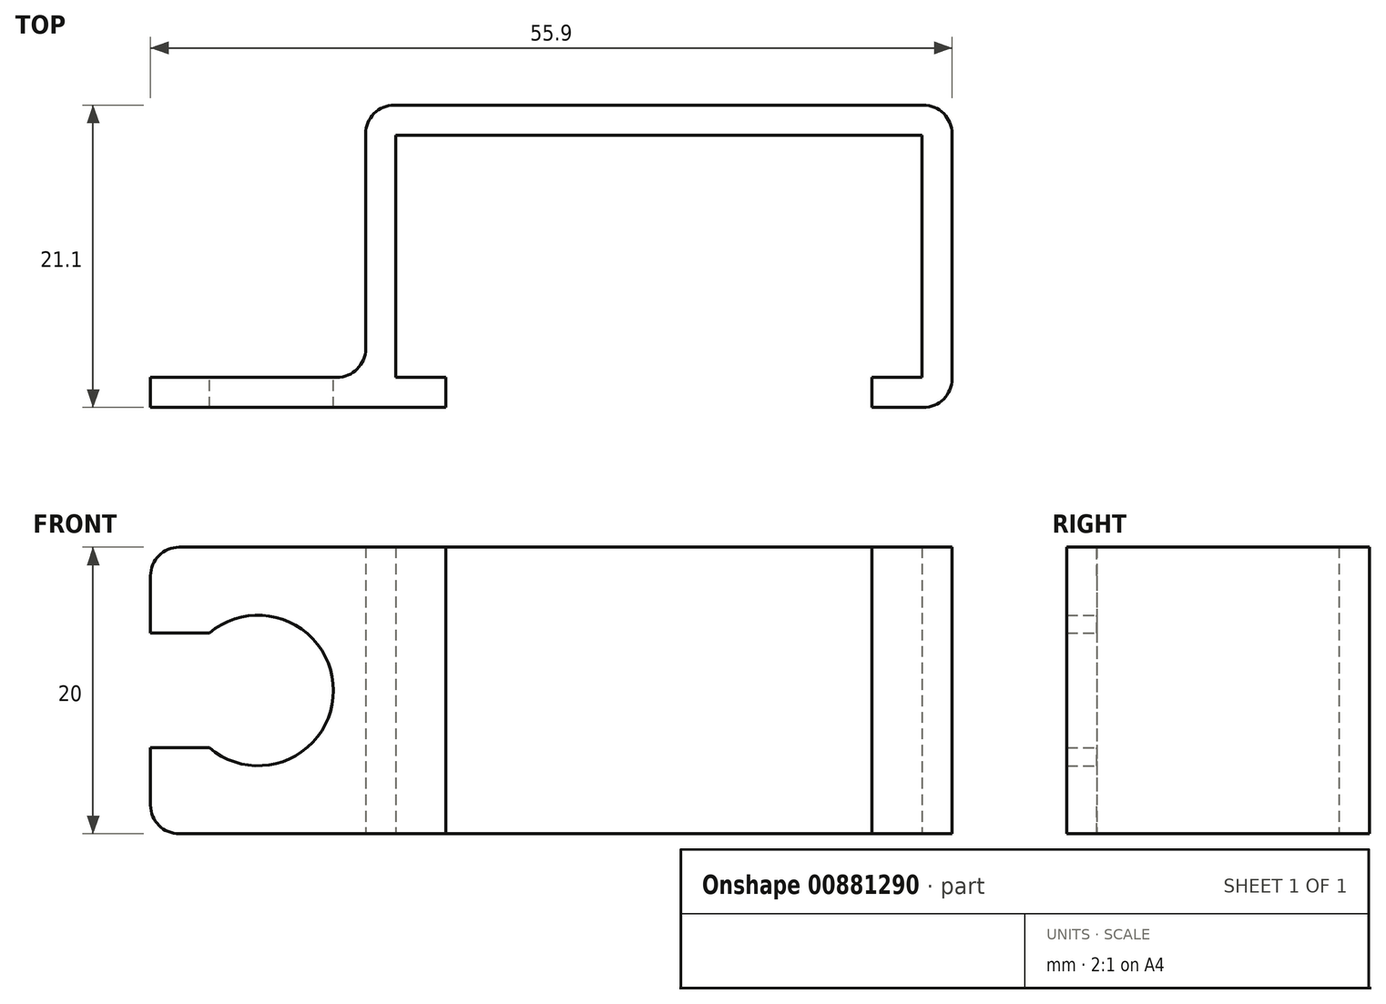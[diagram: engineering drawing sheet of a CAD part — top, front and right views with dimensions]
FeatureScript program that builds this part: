
annotation { "Feature Type Name" : "Feature", "Feature Type Description" : "" }
export const myFeature = defineFeature(function(context is Context, id is Id, definition is map)
    precondition{}
    {
        {
            var Q0;
            Q0=qCreatedBy(makeId("Top.planeOp"),FACE);
            var sketch = newSketch(context, id + "F0", { "sketchPlane" : qUnion([Q0]), "disableImprinting" : false});
            skLineSegment(sketch, "E0.bottom", {"start": v(20.45, -10.55) * mm, "end": v(-20.45, -10.55) * mm});
            skLineSegment(sketch, "E0.top", {"start": v(20.45, 10.55) * mm, "end": v(-20.45, 10.55) * mm});
            skLineSegment(sketch, "E0.left", {"start": v(20.45, -10.55) * mm, "end": v(20.45, 10.55) * mm});
            skLineSegment(sketch, "E0.right", {"start": v(-20.45, -10.55) * mm, "end": v(-20.45, 10.55) * mm});
            skPoint(sketch, "E0.middle", {"position": v(0, 0) * mm});
            skLineSegment(sketch, "E1.0", {"start": v(18.35, 8.45) * mm, "end": v(-18.35, 8.45) * mm});
            skLineSegment(sketch, "E1.1", {"start": v(18.35, -8.45) * mm, "end": v(18.35, 8.45) * mm});
            skLineSegment(sketch, "E1.2", {"start": v(18.35, -8.45) * mm, "end": v(-18.35, -8.45) * mm});
            skLineSegment(sketch, "E1.3", {"start": v(-18.35, -8.45) * mm, "end": v(-18.35, 8.45) * mm});
            skPoint(sketch, "E2", {"position": v(-35.45, -10.55) * mm});
            skPoint(sketch, "E3", {"position": v(-35.45, -8.45) * mm});
            skLineSegment(sketch, "E4", {"start": v(-35.45, -8.45) * mm, "end": v(-20.45, -8.45) * mm});
            skLineSegment(sketch, "E5", {"start": v(-35.45, -8.45) * mm, "end": v(-35.45, -10.55) * mm});
            skLineSegment(sketch, "E6", {"start": v(-35.45, -10.55) * mm, "end": v(-20.45, -10.55) * mm});
            skPoint(sketch, "E7", {"position": v(-14.85, -8.45) * mm});
            skPoint(sketch, "E8", {"position": v(-14.85, -10.55) * mm});
            skPoint(sketch, "E9", {"position": v(14.85, -8.45) * mm});
            skPoint(sketch, "E10", {"position": v(14.85, -10.55) * mm});
            skLineSegment(sketch, "E11", {"start": v(-14.85, -8.45) * mm, "end": v(-14.85, -10.55) * mm});
            skLineSegment(sketch, "E12", {"start": v(14.85, -8.45) * mm, "end": v(14.85, -10.55) * mm});
            skSolve(sketch);
        }
        {
            var Q0;
            {var subQ2=sQuery(id+"F0.wireOp",EDGE,"E4");Q0=makeQuery(id+"F0.imprint","IMPRINT",FACE,{"disambiguationData":[TD([[makeQuery(id+"F0.imprint","IMPRINT",EDGE,{"derivedFrom":subQ2}),-1.0]])]});}
            var Q1;
            {var subQ4=sQuery(id+"F0.wireOp",EDGE,"E0.top");Q1=makeQuery(id+"F0.imprint","IMPRINT",FACE,{"disambiguationData":[TD([[makeQuery(id+"F0.imprint","IMPRINT",EDGE,{"derivedFrom":subQ4}),1.0]])]});}
            extrude(context, id + "F1", {"entities" : qUnion([Q0, Q1]), "depth" : 20 * mm, "offsetDistance" : 25 * mm});
        }
        {
            var Q0;
            Q0=makeQuery(id+"F1.opExtrude","SWEPT_FACE",FACE,{"disambiguationData":[OSD([sQuery(id+"F0.wireOp",EDGE,"E4")])]});
            var sketch = newSketch(context, id + "F2", { "sketchPlane" : qUnion([Q0])});
            skPoint(sketch, "E13", {"position": v(27.95, 10) * mm});
            skPoint(sketch, "E13.positionSnap0", {"position": v(27.95, 0) * mm});
            skPoint(sketch, "E13.positionSnap1", {"position": v(20.45, 10) * mm});
            skCircle(sketch, "E14", {"center": v(27.95, 10) * mm, "radius": 5.25 * mm});
            skPoint(sketch, "E15", {"position": v(35.45, 10) * mm});
            skPoint(sketch, "E16", {"position": v(35.45, 6) * mm});
            skPoint(sketch, "E17", {"position": v(35.45, 14) * mm});
            skLineSegment(sketch, "E18", {"start": v(35.45, 6) * mm, "end": v(31.35, 6) * mm});
            skLineSegment(sketch, "E19", {"start": v(31.35, 6) * mm, "end": v(31.35, 14) * mm});
            skLineSegment(sketch, "E20", {"start": v(31.35, 14) * mm, "end": v(35.45, 14) * mm});
            skSolve(sketch);
        }
        {
            var Q0;
            {var subQ1=sQuery(id+"F2.wireOp",EDGE,"E18");Q0=makeQuery(id+"F2.imprint","IMPRINT",FACE,{"disambiguationData":[TD([[makeQuery(id+"F2.imprint","IMPRINT",EDGE,{"derivedFrom":subQ1}),-1.0]])]});}
            var Q1;
            {var subQ0=sQuery(id+"F2.wireOp",EDGE,"E19");Q1=makeQuery(id+"F2.imprint","IMPRINT",FACE,{"disambiguationData":[TD([[makeQuery(id+"F2.imprint","IMPRINT",EDGE,{"derivedFrom":subQ0}),1.0]])]});}
            var Q2;
            {var subQ0=sQuery(id+"F2.wireOp",EDGE,"E19");Q2=makeQuery(id+"F2.imprint","IMPRINT",FACE,{"disambiguationData":[TD([[makeQuery(id+"F2.imprint","IMPRINT",EDGE,{"derivedFrom":subQ0}),-1.0]])]});}
            extrude(context, id + "F3", {"entities" : qUnion([Q0, Q1, Q2]), "operationType" : NewBodyOperationType.REMOVE, "oppositeDirection" : true, "depth" : 25 * mm, "offsetDistance" : 25 * mm});
        }
        {
            var Q0;
            Q0=makeQuery(id+"F1.opExtrude","SWEPT_EDGE",EDGE,{"disambiguationData":[OSD([sQuery(id+"F0.wireOp",EDGE,"E0.right"),sQuery(id+"F0.wireOp",EDGE,"E4")])]});
            var Q1;
            Q1=makeQuery(id+"F1.opExtrude","SWEPT_EDGE",EDGE,{"disambiguationData":[OSD([sQuery(id+"F0.wireOp",EDGE,"E0.top"),sQuery(id+"F0.wireOp",EDGE,"E0.right")])]});
            var Q2;
            Q2=makeQuery(id+"F1.opExtrude","SWEPT_EDGE",EDGE,{"disambiguationData":[OSD([sQuery(id+"F0.wireOp",EDGE,"E0.top"),sQuery(id+"F0.wireOp",EDGE,"E0.left")])]});
            var Q3;
            Q3=makeQuery(id+"F1.opExtrude","SWEPT_EDGE",EDGE,{"disambiguationData":[OSD([sQuery(id+"F0.wireOp",EDGE,"E0.bottom"),sQuery(id+"F0.wireOp",EDGE,"E0.left")])]});
            var Q4;
            Q4=makeQuery(id+"F1.opExtrude","CAP_EDGE",EDGE,{"disambiguationData":[OSD([sQuery(id+"F0.wireOp",EDGE,"E5")])],"isStart":false});
            var Q5;
            Q5=makeQuery(id+"F1.opExtrude","CAP_EDGE",EDGE,{"disambiguationData":[OSD([sQuery(id+"F0.wireOp",EDGE,"E5")])],"isStart":true});
            var Q6;
            Q6=makeQuery(id+"F3.boolean.opBoolean","COPY",EDGE,{"derivedFrom":makeQuery(id+"F3.opExtrude","SWEPT_EDGE",EDGE,{"disambiguationData":[OSD([sQuery(id+"F0.wireOp",EDGE,"E4"),sQuery(id+"F0.wireOp",EDGE,"E5"),sQuery(id+"F2.wireOp",EDGE,"E18")])]})});
            var Q7;
            Q7=makeQuery(id+"F3.boolean.opBoolean","COPY",EDGE,{"derivedFrom":makeQuery(id+"F3.opExtrude","SWEPT_EDGE",EDGE,{"disambiguationData":[OSD([sQuery(id+"F0.wireOp",EDGE,"E4"),sQuery(id+"F0.wireOp",EDGE,"E5"),sQuery(id+"F2.wireOp",EDGE,"E20")])]})});
            fillet(context, id + "F4", {"entities" : qUnion([Q0, Q1, Q2, Q3, Q4, Q5, Q6, Q7]), "radius" : 2 * mm, "tangentPropagation" : true, "allowEdgeOverflow" : false});
        }
    });
